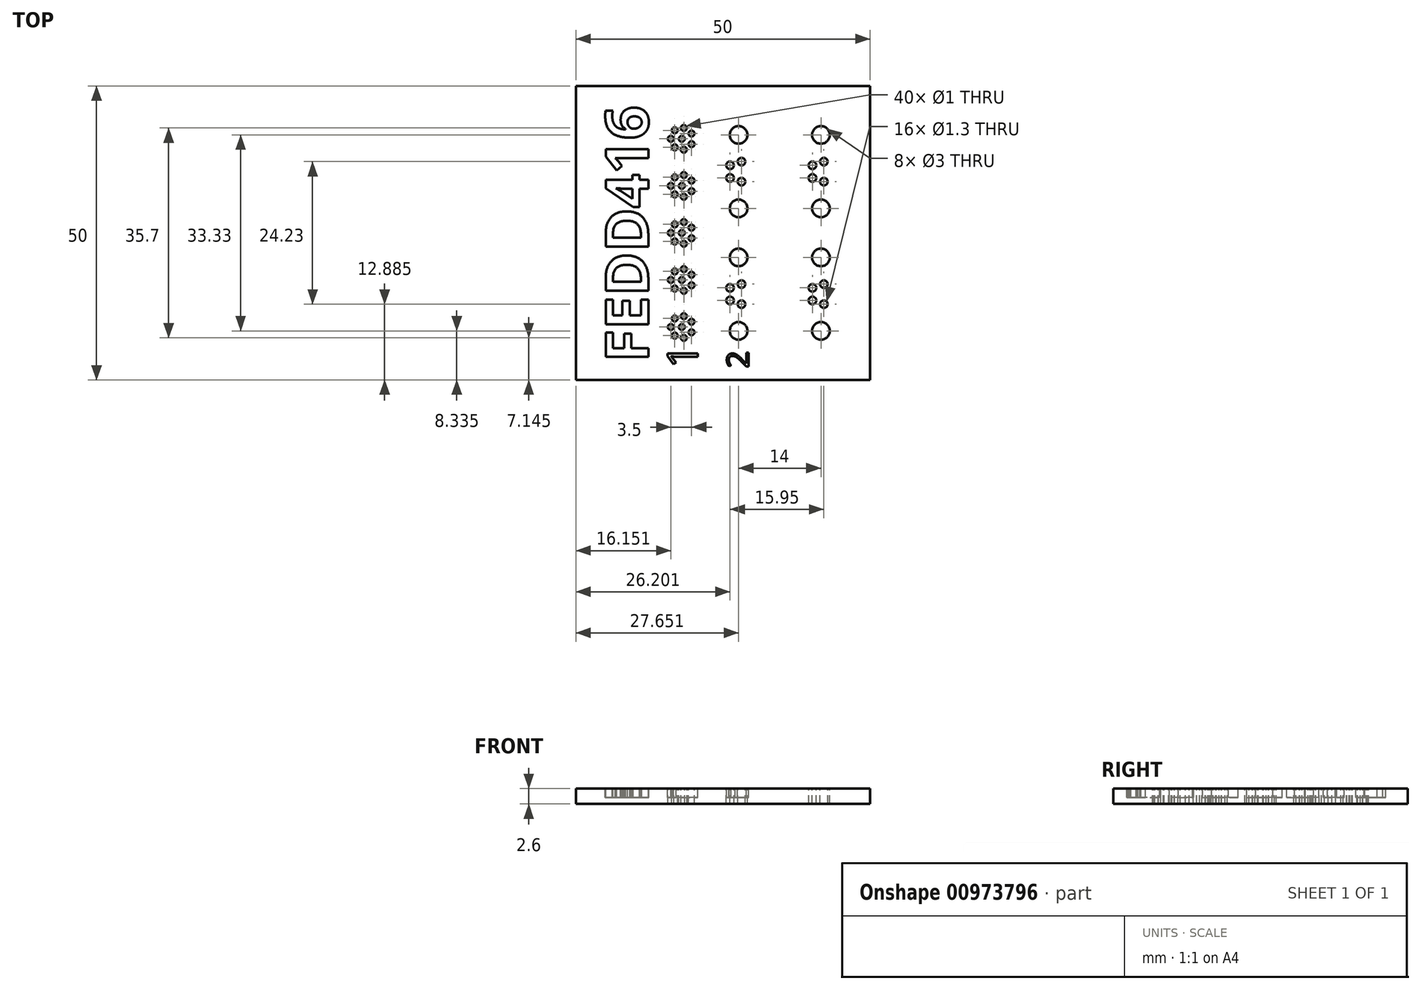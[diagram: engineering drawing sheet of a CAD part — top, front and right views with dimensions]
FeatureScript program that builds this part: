
annotation { "Feature Type Name" : "Feature", "Feature Type Description" : "" }
export const myFeature = defineFeature(function(context is Context, id is Id, definition is map)
    precondition{}
    {
        {
            var Q0;
            Q0=qCreatedBy(makeId("Top.planeOp"),FACE);
            var sketch = newSketch(context, id + "F0", { "sketchPlane" : qUnion([Q0])});
            skLineSegment(sketch, "E0.bottom", {"start": v(-43.16, 28.34) * mm, "end": v(6.84, 28.34) * mm});
            skLineSegment(sketch, "E0.top", {"start": v(-43.16, -21.66) * mm, "end": v(6.84, -21.66) * mm});
            skLineSegment(sketch, "E0.left", {"start": v(-43.16, 28.34) * mm, "end": v(-43.16, -21.66) * mm});
            skLineSegment(sketch, "E0.right", {"start": v(6.84, 28.34) * mm, "end": v(6.84, -21.66) * mm});
            skSolve(sketch);
        }
        {
            var Q0;
            Q0=makeQuery(id+"F0.imprint","IMPRINT",FACE,{"disambiguationData":[TD([[makeQuery(id+"F0.imprint","IMPRINT",EDGE,{"derivedFrom":sQuery(id+"F0.wireOp",EDGE,"E0.bottom")}),-1.0]])]});
            extrude(context, id + "F1", {"entities" : qUnion([Q0]), "depth" : 2.6 * mm, "offsetDistance" : 25 * mm});
        }
        {
            var Q0;
            Q0=makeQuery(id+"F1.opExtrude","CAP_FACE",FACE,{"disambiguationData":[OSD([sQuery(id+"F0.wireOp",EDGE,"E0.bottom"),sQuery(id+"F0.wireOp",EDGE,"E0.top"),sQuery(id+"F0.wireOp",EDGE,"E0.left"),sQuery(id+"F0.wireOp",EDGE,"E0.right")])],"isStart":false});
            var sketch = newSketch(context, id + "F2", { "sketchPlane" : qUnion([Q0])});
            skText(sketch, "E1", { "text": "FEDD416", "fontName": "OpenSans-Bold.ttf"});
            skText(sketch, "E2", { "text": "1", "fontName": "OpenSans-Regular.ttf"});
            skText(sketch, "E3", { "text": "2\n", "fontName": "OpenSans-Regular.ttf"});
            const initialGuessF2  = {"E1": [-0.03085, -0.01866, 0, 1, 0.0073], "E2": [-0.02242, -0.01966, 0, 1, 0.00522], "E3": [-0.0138, -0.01966, 0, 1, 0.0037]};
            skSetInitialGuess(sketch, initialGuessF2);
            skSolve(sketch);
        }
        {
            var Q0;
            Q0=qSketchRegion(id+"F2",true);
            extrude(context, id + "F3", {"entities" : qUnion([Q0]), "operationType" : NewBodyOperationType.REMOVE, "oppositeDirection" : true, "depth" : 1.5 * mm, "offsetDistance" : 25 * mm});
        }
        {
            var Q0;
            {var subQ0=sQuery(id+"F0.wireOp",EDGE,"E0.left");var subQ1=sQuery(id+"F0.wireOp",EDGE,"E0.bottom");var subQ2=sQuery(id+"F0.wireOp",EDGE,"E0.right");var subQ3=sQuery(id+"F0.wireOp",EDGE,"E0.top");Q0=makeQuery(id+"F3.boolean.opBoolean","SPLIT",FACE,{"disambiguationData":[TD([makeQuery(id+"F1.opExtrude","SWEPT_FACE",FACE,{"disambiguationData":[OSD([subQ1])]})])],"derivedFrom":makeQuery(id+"F1.opExtrude","CAP_FACE",FACE,{"disambiguationData":[OSD([subQ1,subQ3,subQ0,subQ2])],"isStart":false})});}
            var sketch = newSketch(context, id + "F4", { "sketchPlane" : qUnion([Q0])});
            skCircle(sketch, "E4", {"center": v(-27, -4.66) * mm, "radius": 0.5 * mm});
            skCircle(sketch, "E5", {"center": v(-25.16, -4.66) * mm, "radius": 0.5 * mm});
            skCircle(sketch, "E6", {"center": v(-26.36, -3.21) * mm, "radius": 0.5 * mm});
            skCircle(sketch, "E7", {"center": v(-24.8, -2.81) * mm, "radius": 0.5 * mm});
            skCircle(sketch, "E8", {"center": v(-23.5, -3.76) * mm, "radius": 0.5 * mm});
            skCircle(sketch, "E9", {"center": v(-23.5, -5.56) * mm, "radius": 0.5 * mm});
            skCircle(sketch, "E10", {"center": v(-24.8, -6.51) * mm, "radius": 0.5 * mm});
            skCircle(sketch, "E11", {"center": v(-26.36, -6.11) * mm, "radius": 0.5 * mm});
            skCircle(sketch, "E12", {"center": v(-27, 3.34) * mm, "radius": 0.5 * mm});
            skCircle(sketch, "E13", {"center": v(-25.16, 3.34) * mm, "radius": 0.5 * mm});
            skCircle(sketch, "E14", {"center": v(-26.36, 4.79) * mm, "radius": 0.5 * mm});
            skCircle(sketch, "E15", {"center": v(-24.8, 5.19) * mm, "radius": 0.5 * mm});
            skCircle(sketch, "E16", {"center": v(-23.5, 4.24) * mm, "radius": 0.5 * mm});
            skCircle(sketch, "E17", {"center": v(-23.5, 2.44) * mm, "radius": 0.5 * mm});
            skCircle(sketch, "E18", {"center": v(-24.8, 1.49) * mm, "radius": 0.5 * mm});
            skCircle(sketch, "E19", {"center": v(-26.36, 1.89) * mm, "radius": 0.5 * mm});
            skCircle(sketch, "E20", {"center": v(-27, -12.66) * mm, "radius": 0.5 * mm});
            skCircle(sketch, "E21", {"center": v(-25.16, -12.66) * mm, "radius": 0.5 * mm});
            skCircle(sketch, "E22", {"center": v(-26.36, -11.21) * mm, "radius": 0.5 * mm});
            skCircle(sketch, "E23", {"center": v(-24.8, -10.81) * mm, "radius": 0.5 * mm});
            skCircle(sketch, "E24", {"center": v(-23.5, -11.76) * mm, "radius": 0.5 * mm});
            skCircle(sketch, "E25", {"center": v(-23.5, -13.56) * mm, "radius": 0.5 * mm});
            skCircle(sketch, "E26", {"center": v(-24.8, -14.51) * mm, "radius": 0.5 * mm});
            skCircle(sketch, "E27", {"center": v(-26.36, -14.11) * mm, "radius": 0.5 * mm});
            skCircle(sketch, "E28", {"center": v(-27, 11.34) * mm, "radius": 0.5 * mm});
            skCircle(sketch, "E29", {"center": v(-25.16, 11.34) * mm, "radius": 0.5 * mm});
            skCircle(sketch, "E30", {"center": v(-26.36, 12.79) * mm, "radius": 0.5 * mm});
            skCircle(sketch, "E31", {"center": v(-24.8, 13.19) * mm, "radius": 0.5 * mm});
            skCircle(sketch, "E32", {"center": v(-23.5, 12.24) * mm, "radius": 0.5 * mm});
            skCircle(sketch, "E33", {"center": v(-23.5, 10.44) * mm, "radius": 0.5 * mm});
            skCircle(sketch, "E34", {"center": v(-24.8, 9.49) * mm, "radius": 0.5 * mm});
            skCircle(sketch, "E35", {"center": v(-26.36, 9.89) * mm, "radius": 0.5 * mm});
            skCircle(sketch, "E36", {"center": v(-27, 19.34) * mm, "radius": 0.5 * mm});
            skCircle(sketch, "E37", {"center": v(-25.16, 19.34) * mm, "radius": 0.5 * mm});
            skCircle(sketch, "E38", {"center": v(-26.36, 20.79) * mm, "radius": 0.5 * mm});
            skCircle(sketch, "E39", {"center": v(-24.8, 21.19) * mm, "radius": 0.5 * mm});
            skCircle(sketch, "E40", {"center": v(-23.5, 20.24) * mm, "radius": 0.5 * mm});
            skCircle(sketch, "E41", {"center": v(-23.5, 18.44) * mm, "radius": 0.5 * mm});
            skCircle(sketch, "E42", {"center": v(-24.8, 17.49) * mm, "radius": 0.5 * mm});
            skCircle(sketch, "E43", {"center": v(-26.36, 17.89) * mm, "radius": 0.5 * mm});
            skCircle(sketch, "E44", {"center": v(-15.5, -13.32) * mm, "radius": 1.5 * mm});
            skCircle(sketch, "E45", {"center": v(-15.5, -0.82) * mm, "radius": 1.5 * mm});
            skCircle(sketch, "E46", {"center": v(-15, -8.77) * mm, "radius": 0.65 * mm});
            skCircle(sketch, "E47", {"center": v(-15, -5.37) * mm, "radius": 0.65 * mm});
            skCircle(sketch, "E48", {"center": v(-16.96, -8.15) * mm, "radius": 0.65 * mm});
            skCircle(sketch, "E49", {"center": v(-16.96, -6) * mm, "radius": 0.65 * mm});
            skCircle(sketch, "E50", {"center": v(-15.5, 7.5) * mm, "radius": 1.5 * mm});
            skCircle(sketch, "E51", {"center": v(-15.5, 20) * mm, "radius": 1.5 * mm});
            skCircle(sketch, "E52", {"center": v(-15, 12.06) * mm, "radius": 0.65 * mm});
            skCircle(sketch, "E53", {"center": v(-15, 15.46) * mm, "radius": 0.65 * mm});
            skCircle(sketch, "E54", {"center": v(-16.96, 12.68) * mm, "radius": 0.65 * mm});
            skCircle(sketch, "E55", {"center": v(-16.96, 14.83) * mm, "radius": 0.65 * mm});
            skCircle(sketch, "E56", {"center": v(-1.5, -13.32) * mm, "radius": 1.5 * mm});
            skCircle(sketch, "E57", {"center": v(-1.5, -0.82) * mm, "radius": 1.5 * mm});
            skCircle(sketch, "E58", {"center": v(-1, -8.77) * mm, "radius": 0.65 * mm});
            skCircle(sketch, "E59", {"center": v(-1, -5.37) * mm, "radius": 0.65 * mm});
            skCircle(sketch, "E60", {"center": v(-2.96, -8.15) * mm, "radius": 0.65 * mm});
            skCircle(sketch, "E61", {"center": v(-2.96, -6) * mm, "radius": 0.65 * mm});
            skCircle(sketch, "E62", {"center": v(-1.5, 7.5) * mm, "radius": 1.5 * mm});
            skCircle(sketch, "E63", {"center": v(-1.5, 20) * mm, "radius": 1.5 * mm});
            skCircle(sketch, "E64", {"center": v(-1, 12.06) * mm, "radius": 0.65 * mm});
            skCircle(sketch, "E65", {"center": v(-1, 15.46) * mm, "radius": 0.65 * mm});
            skCircle(sketch, "E66", {"center": v(-2.96, 12.68) * mm, "radius": 0.65 * mm});
            skCircle(sketch, "E67", {"center": v(-2.96, 14.83) * mm, "radius": 0.65 * mm});
            skSolve(sketch);
        }
        {
            var Q0;
            Q0 = qSketchRegion(id + "F4", true);
            extrude(context, id + "F5", {"entities" : qUnion([Q0]), "operationType" : NewBodyOperationType.REMOVE, "endBound" : BoundingType.UP_TO_NEXT, "oppositeDirection" : true, "depth" : 25 * mm, "offsetDistance" : 25 * mm});
        }
    });
